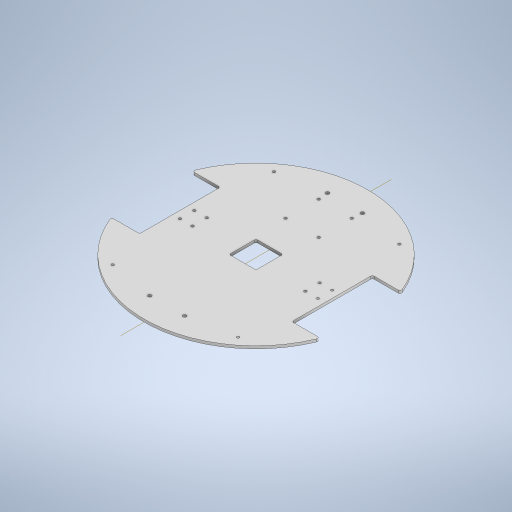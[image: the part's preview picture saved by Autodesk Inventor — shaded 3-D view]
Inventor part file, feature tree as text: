
AUTODESK INVENTOR PART (.ipt)
format: ipt  version: 2023.3 (Build 273359000, 359)  size: 281,600 bytes
history: native  units: mm
features: extrude x1
ambient origin geometry x8: Origin, YZ Plane, XZ Plane, XY Plane, X Axis, Y Axis, Z Axis, Center Point
bodies: Body1 (feature_tree)
feature tree (1):
  extrude  "Extrusion2"  Depth=250.0mm
